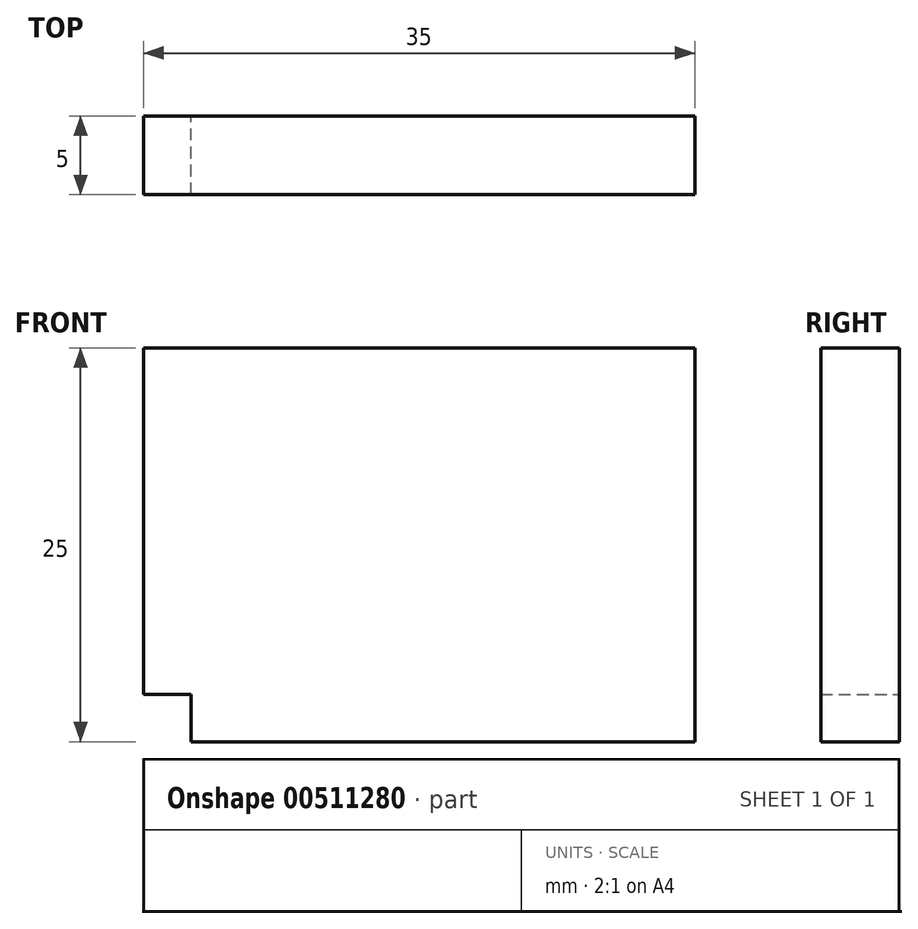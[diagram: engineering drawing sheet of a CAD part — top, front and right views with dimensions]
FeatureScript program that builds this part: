
annotation { "Feature Type Name" : "Feature", "Feature Type Description" : "" }
export const myFeature = defineFeature(function(context is Context, id is Id, definition is map)
    precondition{}
    {
        {
            var Q0;
            Q0=qCreatedBy(makeId("Front.planeOp"),FACE);
            var sketch = newSketch(context, id + "F0", { "sketchPlane" : qUnion([Q0])});
            skLineSegment(sketch, "E0", {"start": v(0, 0) * mm, "end": v(3, 0) * mm});
            skLineSegment(sketch, "E1", {"start": v(3, 0) * mm, "end": v(3, -3) * mm});
            skLineSegment(sketch, "E2", {"start": v(3, -3) * mm, "end": v(35, -3) * mm});
            skLineSegment(sketch, "E3", {"start": v(35, -3) * mm, "end": v(35, 22) * mm});
            skLineSegment(sketch, "E4", {"start": v(35, 22) * mm, "end": v(0, 22) * mm});
            skLineSegment(sketch, "E5", {"start": v(0, 22) * mm, "end": v(0, 0) * mm});
            skSolve(sketch);
        }
        {
            var Q0;
            Q0 = qSketchRegion(id + "F0", true);
            extrude(context, id + "F1", {"entities" : qUnion([Q0]), "depth" : 5 * mm});
        }
    });
